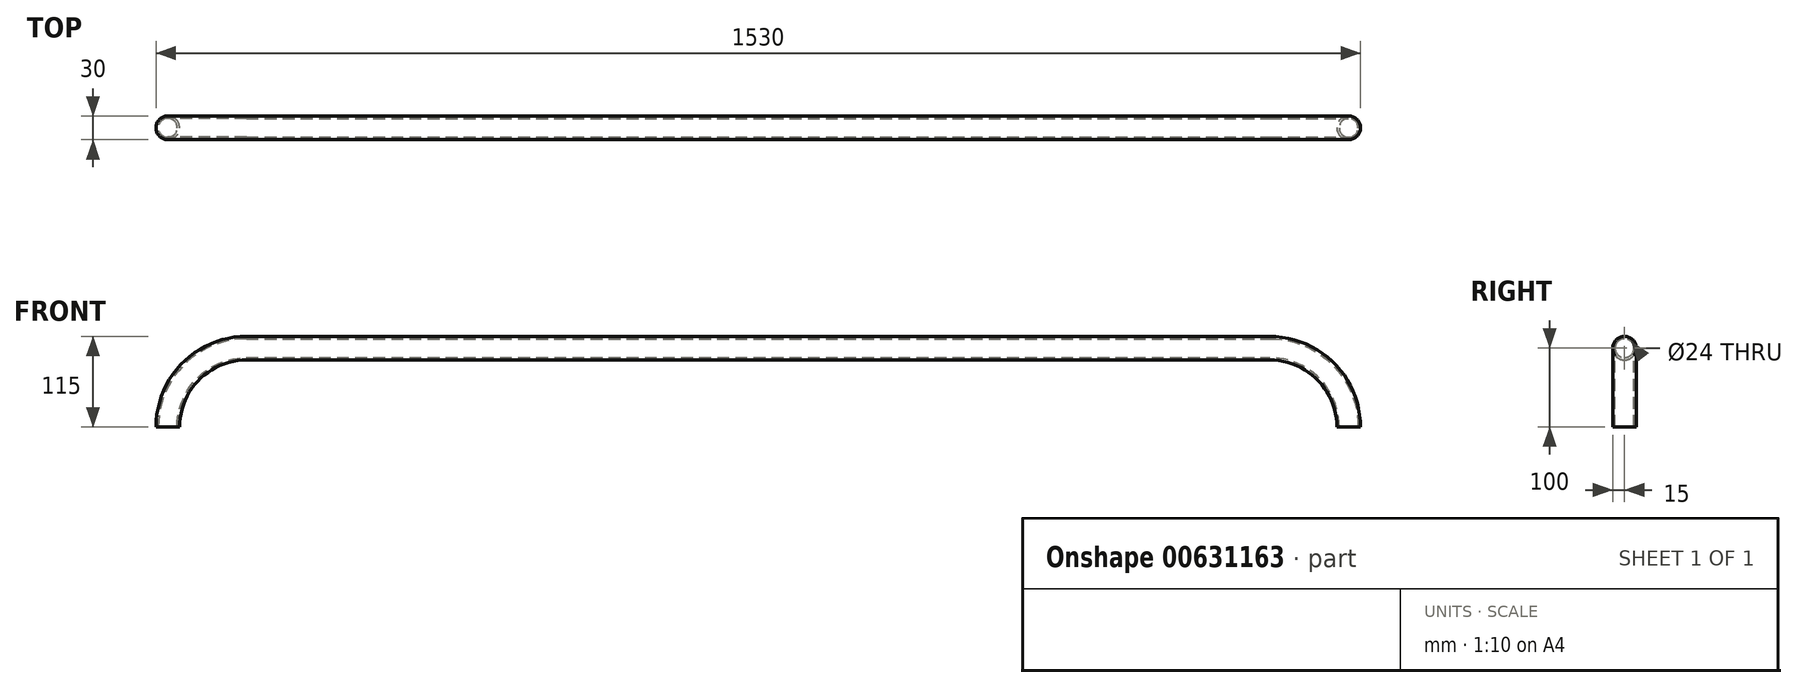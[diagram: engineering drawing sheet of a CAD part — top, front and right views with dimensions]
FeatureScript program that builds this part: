
annotation { "Feature Type Name" : "Feature", "Feature Type Description" : "" }
export const myFeature = defineFeature(function(context is Context, id is Id, definition is map)
    precondition{}
    {
        {
            var Q0;
            Q0=qCreatedBy(makeId("Front.planeOp"),FACE);
            var sketch = newSketch(context, id + "F0", { "sketchPlane" : qUnion([Q0])});
            skLineSegment(sketch, "E0", {"start": v(0, 0) * mm, "end": v(0, 1500) * mm, "construction": true});
            skLineSegment(sketch, "E1", {"start": v(0, 0) * mm, "end": v(-750, 0) * mm, "construction": true});
            skLineSegment(sketch, "E2", {"start": v(0, 0) * mm, "end": v(750, 0) * mm, "construction": true});
            skLineSegment(sketch, "E3", {"start": v(0, 1500) * mm, "end": v(-650, 1500) * mm});
            skLineSegment(sketch, "E4", {"start": v(0, 1500) * mm, "end": v(650, 1500) * mm});
            skLineSegment(sketch, "E5", {"start": v(-750, 0) * mm, "end": v(-750, 1400) * mm, "construction": true});
            skLineSegment(sketch, "E6", {"start": v(750, 0) * mm, "end": v(750, 1400) * mm, "construction": true});
            skArc(sketch, "E7", {"start": v(-650, 1500) * mm, "mid": v(-720.71, 1470.71) * mm, "end": v(-750, 1400) * mm});
            skArc(sketch, "E8", {"start": v(650, 1500) * mm, "mid": v(720.71, 1470.71) * mm, "end": v(750, 1400) * mm});
            skSolve(sketch);
        }
        {
            var Q0;
            Q0=qCreatedBy(makeId("Right.planeOp"),FACE);
            var sketch = newSketch(context, id + "F1", { "sketchPlane" : qUnion([Q0])});
            skCircle(sketch, "E9", {"center": v(0, 1500) * mm, "radius": 15 * mm});
            skSolve(sketch);
        }
        {
            var Q0;
            Q0=makeQuery(id+"F1.imprint","IMPRINT",FACE,{"disambiguationData":[TD([[makeQuery(id+"F1.imprint","IMPRINT",EDGE,{"derivedFrom":sQuery(id+"F1.wireOp",EDGE,"E9")}),1.0]])]});
            var Q1;
            Q1=sQuery(id+"F0.wireOp",EDGE,"E8");
            var Q2;
            Q2=sQuery(id+"F0.wireOp",EDGE,"E4");
            var Q3;
            Q3=sQuery(id+"F0.wireOp",EDGE,"E3");
            var Q4;
            Q4=sQuery(id+"F0.wireOp",EDGE,"E7");
            sweep(context, id + "F2", {"profiles" : qUnion([Q0]), "path" : qUnion([Q1, Q2, Q3, Q4])});
        }
        {
            var Q0;
            Q0=makeQuery(id+"F2.opSweep","CAP_FACE",FACE,{"disambiguationData":[OSD([sQuery(id+"F0.wireOp",VERTEX,"E7.end"),sQuery(id+"F1.wireOp",EDGE,"E9")])],"isStart":true});
            var Q1;
            Q1=makeQuery(id+"F2.opSweep","CAP_FACE",FACE,{"disambiguationData":[OSD([sQuery(id+"F0.wireOp",VERTEX,"E8.end"),sQuery(id+"F1.wireOp",EDGE,"E9")])],"isStart":false});
            shell(context, id + "F3", {"entities" : qUnion([Q0, Q1]), "thickness" : 3 * mm});
        }
    });
